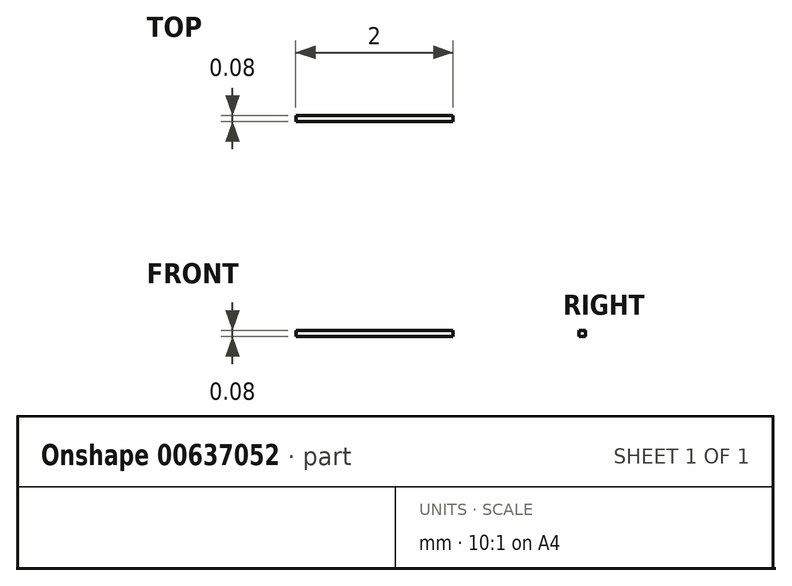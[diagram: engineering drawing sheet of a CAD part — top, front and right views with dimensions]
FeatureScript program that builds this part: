
annotation { "Feature Type Name" : "Feature", "Feature Type Description" : "" }
export const myFeature = defineFeature(function(context is Context, id is Id, definition is map)
    precondition{}
    {
        {
            var Q0;
            Q0=qCreatedBy(makeId("Top.planeOp"),FACE);
            var sketch = newSketch(context, id + "F0", { "sketchPlane" : qUnion([Q0])});
            skLineSegment(sketch, "E0.bottom", {"start": v(-1, -0.04) * mm, "end": v(1, -0.04) * mm});
            skLineSegment(sketch, "E0.top", {"start": v(-1, 0.04) * mm, "end": v(1, 0.04) * mm});
            skLineSegment(sketch, "E0.left", {"start": v(-1, -0.04) * mm, "end": v(-1, 0.04) * mm});
            skLineSegment(sketch, "E0.right", {"start": v(1, -0.04) * mm, "end": v(1, 0.04) * mm});
            skPoint(sketch, "E0.middle", {"position": v(0, 0) * mm});
            skSolve(sketch);
        }
        {
            var Q0;
            Q0 = qSketchRegion(id + "F0", true);
            extrude(context, id + "F1", {"entities" : qUnion([Q0]), "depth" : 0.08 * mm, "offsetDistance" : 25 * mm});
        }
    });
